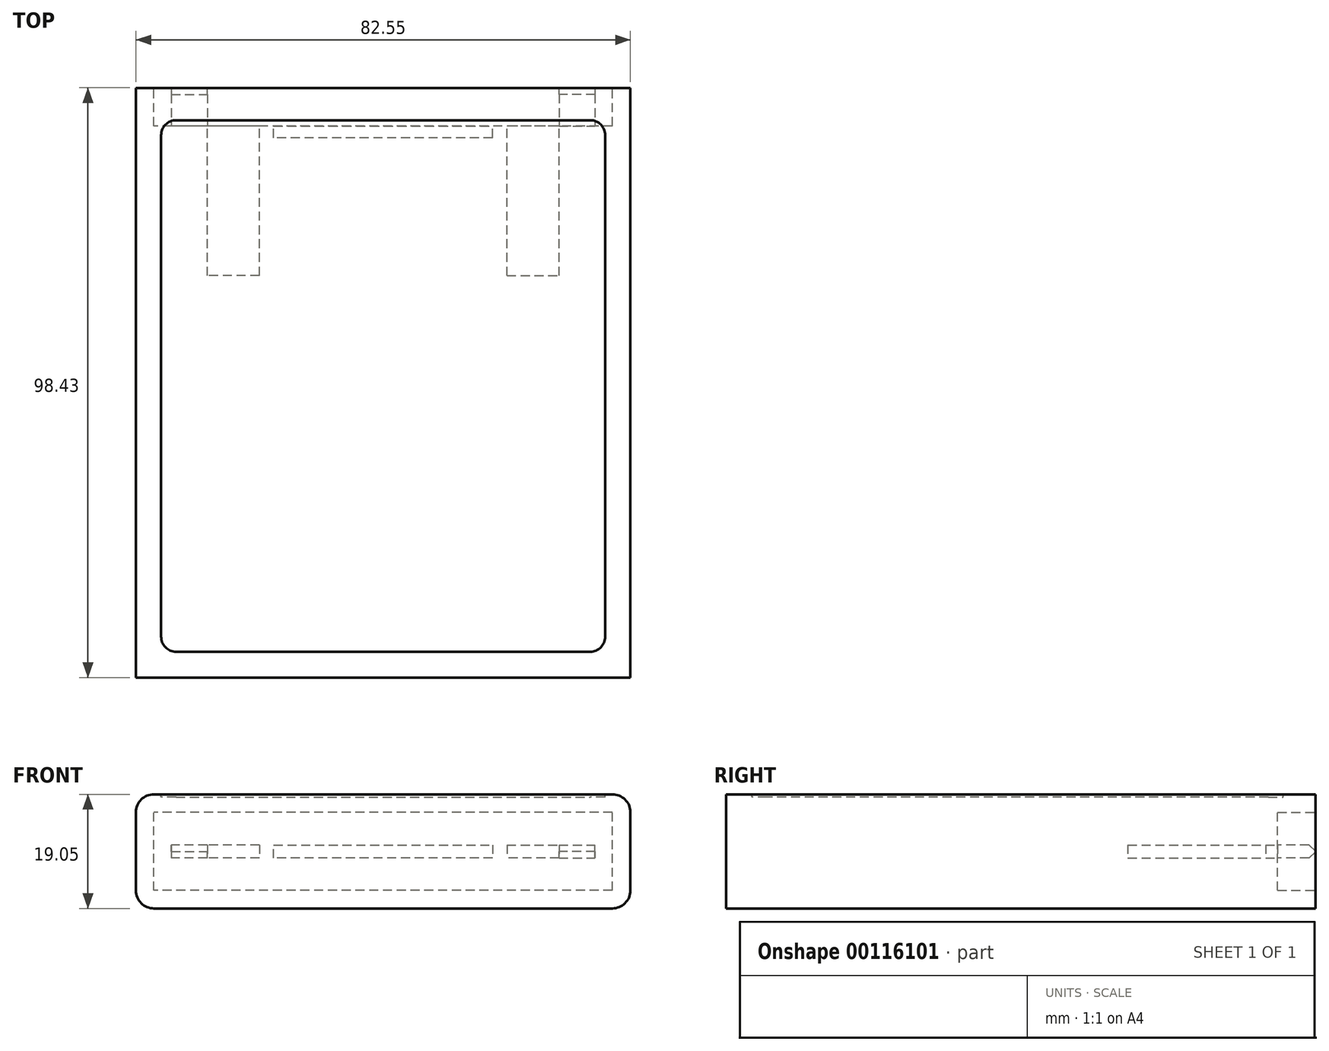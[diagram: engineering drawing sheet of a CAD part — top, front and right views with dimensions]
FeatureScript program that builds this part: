
annotation { "Feature Type Name" : "Feature", "Feature Type Description" : "" }
export const myFeature = defineFeature(function(context is Context, id is Id, definition is map)
    precondition{}
    {
        {
            var Q0;
            Q0=qCreatedBy(makeId("Top.planeOp"),FACE);
            var sketch = newSketch(context, id + "F0", { "sketchPlane" : qUnion([Q0])});
            skLineSegment(sketch, "E0.bottom", {"start": v(0, 0) * mm, "end": v(-82.55, 0) * mm});
            skLineSegment(sketch, "E0.top", {"start": v(0, 98.42) * mm, "end": v(-82.55, 98.42) * mm});
            skLineSegment(sketch, "E0.left", {"start": v(0, 0) * mm, "end": v(0, 98.42) * mm});
            skLineSegment(sketch, "E0.right", {"start": v(-82.55, 0) * mm, "end": v(-82.55, 98.42) * mm});
            skSolve(sketch);
        }
        {
            var Q0;
            Q0=makeQuery(id+"F0.imprint","IMPRINT",FACE,{"disambiguationData":[TD([[makeQuery(id+"F0.imprint","IMPRINT",EDGE,{"derivedFrom":sQuery(id+"F0.wireOp",EDGE,"E0.bottom")}),-1.0]])]});
            var sketch = newSketch(context, id + "F1", { "sketchPlane" : qUnion([Q0])});
            skSolve(sketch);
        }
        {
            var Q0;
            Q0 = qSketchRegion(id + "F1", true);
            var Q1;
            Q1=makeQuery(id+"F0.imprint","IMPRINT",FACE,{"disambiguationData":[TD([[makeQuery(id+"F0.imprint","IMPRINT",EDGE,{"derivedFrom":sQuery(id+"F0.wireOp",EDGE,"E0.bottom")}),-1.0]])]});
            extrude(context, id + "F2", {"entities" : qUnion([Q0, Q1]), "oppositeDirection" : true, "depth" : 19.05 * mm});
        }
        {
            var Q0;
            Q0=makeQuery(id+"F2.opExtrude","CAP_EDGE",EDGE,{"disambiguationData":[OSD([sQuery(id+"F0.wireOp",EDGE,"E0.right")])],"isStart":false});
            var Q1;
            Q1=makeQuery(id+"F2.opExtrude","CAP_EDGE",EDGE,{"disambiguationData":[OSD([sQuery(id+"F0.wireOp",EDGE,"E0.right")])],"isStart":true});
            var Q2;
            Q2=makeQuery(id+"F2.opExtrude","CAP_EDGE",EDGE,{"disambiguationData":[OSD([sQuery(id+"F0.wireOp",EDGE,"E0.left")])],"isStart":true});
            var Q3;
            Q3=makeQuery(id+"F2.opExtrude","CAP_EDGE",EDGE,{"disambiguationData":[OSD([sQuery(id+"F0.wireOp",EDGE,"E0.left")])],"isStart":false});
            fillet(context, id + "F3", {"entities" : qUnion([Q0, Q1, Q2, Q3]), "radius" : 3 * mm, "tangentPropagation" : true, "allowEdgeOverflow" : false});
        }
        {
            var Q0;
            Q0=makeQuery(id+"F2.opExtrude","SWEPT_FACE",FACE,{"disambiguationData":[OSD([sQuery(id+"F0.wireOp",EDGE,"E0.top")])]});
            var sketch = newSketch(context, id + "F4", { "sketchPlane" : qUnion([Q0])});
            skLineSegment(sketch, "E1.bottom", {"start": v(3, -16.05) * mm, "end": v(79.55, -16.05) * mm});
            skLineSegment(sketch, "E1.top", {"start": v(3, -3) * mm, "end": v(79.55, -3) * mm});
            skLineSegment(sketch, "E1.left", {"start": v(3, -16.05) * mm, "end": v(3, -3) * mm});
            skLineSegment(sketch, "E1.right", {"start": v(79.55, -16.05) * mm, "end": v(79.55, -3) * mm});
            skSolve(sketch);
        }
        {
            var Q0;
            Q0 = qSketchRegion(id + "F4", true);
            extrude(context, id + "F5", {"entities" : qUnion([Q0]), "operationType" : NewBodyOperationType.REMOVE, "oppositeDirection" : true, "depth" : 6.35 * mm});
        }
        {
            var Q0;
            Q0=makeQuery(id+"F5.boolean.opBoolean","COPY",FACE,{"derivedFrom":makeQuery(id+"F5.opExtrude","CAP_FACE",FACE,{"disambiguationData":[OSD([sQuery(id+"F4.wireOp",EDGE,"E1.bottom"),sQuery(id+"F4.wireOp",EDGE,"E1.top"),sQuery(id+"F4.wireOp",EDGE,"E1.left"),sQuery(id+"F4.wireOp",EDGE,"E1.right")])],"isStart":false})});
            var sketch = newSketch(context, id + "F6", { "sketchPlane" : qUnion([Q0])});
            skLineSegment(sketch, "E2", {"start": v(23, -10.65) * mm, "end": v(59.55, -10.65) * mm});
            skLineSegment(sketch, "E3", {"start": v(59.55, -10.65) * mm, "end": v(59.55, -8.45) * mm});
            skLineSegment(sketch, "E4", {"start": v(59.55, -8.45) * mm, "end": v(23, -8.45) * mm});
            skLineSegment(sketch, "E5", {"start": v(23, -8.45) * mm, "end": v(23, -10.65) * mm});
            skSolve(sketch);
        }
        {
            var Q0;
            Q0 = qSketchRegion(id + "F6", true);
            extrude(context, id + "F7", {"entities" : qUnion([Q0]), "operationType" : NewBodyOperationType.REMOVE, "oppositeDirection" : true, "depth" : 2 * mm});
        }
        {
            var Q0;
            Q0=makeQuery(id+"F5.boolean.opBoolean","COPY",FACE,{"derivedFrom":makeQuery(id+"F5.opExtrude","CAP_FACE",FACE,{"disambiguationData":[OSD([sQuery(id+"F4.wireOp",EDGE,"E1.bottom"),sQuery(id+"F4.wireOp",EDGE,"E1.top"),sQuery(id+"F4.wireOp",EDGE,"E1.left"),sQuery(id+"F4.wireOp",EDGE,"E1.right")])],"isStart":false})});
            var sketch = newSketch(context, id + "F8", { "sketchPlane" : qUnion([Q0])});
            skPoint(sketch, "E6.firstSnap0", {"position": v(41.27, -8.45) * mm});
            skLineSegment(sketch, "E6.bottom", {"start": v(61.95, -8.45) * mm, "end": v(70.65, -8.45) * mm});
            skLineSegment(sketch, "E6.top", {"start": v(61.95, -10.65) * mm, "end": v(70.65, -10.65) * mm});
            skLineSegment(sketch, "E6.left", {"start": v(61.95, -8.45) * mm, "end": v(61.95, -10.65) * mm});
            skLineSegment(sketch, "E6.right", {"start": v(70.65, -8.45) * mm, "end": v(70.65, -10.65) * mm});
            skPoint(sketch, "E7.firstSnap0", {"position": v(66.3, -8.45) * mm});
            skLineSegment(sketch, "E7.bottom", {"start": v(20.6, -8.45) * mm, "end": v(11.9, -8.45) * mm});
            skLineSegment(sketch, "E7.left", {"start": v(20.6, -8.45) * mm, "end": v(20.6, -10.65) * mm});
            skLineSegment(sketch, "E7.right", {"start": v(11.9, -8.45) * mm, "end": v(11.9, -10.65) * mm});
            skLineSegment(sketch, "E8", {"start": v(11.9, -10.65) * mm, "end": v(20.6, -10.65) * mm});
            skSolve(sketch);
        }
        {
            var Q0;
            Q0 = qSketchRegion(id + "F8", true);
            extrude(context, id + "F9", {"entities" : qUnion([Q0]), "operationType" : NewBodyOperationType.REMOVE, "oppositeDirection" : true, "depth" : 25 * mm});
        }
        {
            var Q0;
            Q0=makeQuery(id+"F5.boolean.opBoolean","COPY",FACE,{"derivedFrom":makeQuery(id+"F5.opExtrude","CAP_FACE",FACE,{"disambiguationData":[OSD([sQuery(id+"F4.wireOp",EDGE,"E1.bottom"),sQuery(id+"F4.wireOp",EDGE,"E1.top"),sQuery(id+"F4.wireOp",EDGE,"E1.left"),sQuery(id+"F4.wireOp",EDGE,"E1.right")])],"isStart":false})});
            var sketch = newSketch(context, id + "F10", { "sketchPlane" : qUnion([Q0])});
            skLineSegment(sketch, "E9.bottom", {"start": v(70.65, -8.45) * mm, "end": v(76.65, -8.45) * mm});
            skLineSegment(sketch, "E9.top", {"start": v(70.65, -10.65) * mm, "end": v(76.65, -10.65) * mm});
            skLineSegment(sketch, "E9.left", {"start": v(70.65, -8.45) * mm, "end": v(70.65, -10.65) * mm});
            skLineSegment(sketch, "E9.right", {"start": v(76.65, -8.45) * mm, "end": v(76.65, -10.65) * mm});
            skLineSegment(sketch, "E10.bottom", {"start": v(11.9, -10.65) * mm, "end": v(5.9, -10.65) * mm});
            skLineSegment(sketch, "E10.top", {"start": v(11.9, -8.45) * mm, "end": v(5.9, -8.45) * mm});
            skLineSegment(sketch, "E10.left", {"start": v(11.9, -10.65) * mm, "end": v(11.9, -8.45) * mm});
            skLineSegment(sketch, "E10.right", {"start": v(5.9, -10.65) * mm, "end": v(5.9, -8.45) * mm});
            skSolve(sketch);
        }
        {
            var Q0;
            Q0 = qSketchRegion(id + "F10", true);
            var Q1;
            Q1=makeQuery(id+"F2.opExtrude","SWEPT_FACE",FACE,{"disambiguationData":[OSD([sQuery(id+"F0.wireOp",EDGE,"E0.top")])]});
            extrude(context, id + "F11", {"entities" : qUnion([Q0]), "operationType" : NewBodyOperationType.ADD, "endBound" : BoundingType.UP_TO_SURFACE, "endBoundEntityFace" : qUnion([Q1]), "depth" : 25 * mm});
        }
        {
            var Q0;
            Q0=makeQuery(id+"F11.opExtrude","CAP_EDGE",EDGE,{"disambiguationData":[OSD([sQuery(id+"F10.wireOp",EDGE,"E10.top")])],"isStart":false});
            var Q1;
            Q1=makeQuery(id+"F11.opExtrude","CAP_EDGE",EDGE,{"disambiguationData":[OSD([sQuery(id+"F10.wireOp",EDGE,"E10.bottom")])],"isStart":false});
            var Q2;
            Q2=makeQuery(id+"F11.opExtrude","CAP_EDGE",EDGE,{"disambiguationData":[OSD([sQuery(id+"F10.wireOp",EDGE,"E9.bottom")])],"isStart":false});
            var Q3;
            Q3=makeQuery(id+"F11.opExtrude","CAP_EDGE",EDGE,{"disambiguationData":[OSD([sQuery(id+"F10.wireOp",EDGE,"E9.top")])],"isStart":false});
            chamfer(context, id + "F12", {"entities" : qUnion([Q0, Q1, Q2, Q3]), "width" : 1.1 * mm, "tangentPropagation" : true});
        }
        {
            var Q0;
            Q0=makeQuery(id+"F1.imprint","IMPRINT",FACE,{"disambiguationData":[TD([[makeQuery(id+"F1.imprint","IMPRINT",EDGE,{"derivedFrom":makeQuery(id+"F0.imprint","IMPRINT",EDGE,{"derivedFrom":sQuery(id+"F0.wireOp",EDGE,"E0.bottom")})}),-1.0]])]});
            var sketch = newSketch(context, id + "F13", { "sketchPlane" : qUnion([Q0])});
            skLineSegment(sketch, "E11", {"start": v(-75.85, 93.02) * mm, "end": v(-6.7, 93.02) * mm});
            skLineSegment(sketch, "E12", {"start": v(-4.2, 90.52) * mm, "end": v(-4.2, 6.8) * mm});
            skLineSegment(sketch, "E13", {"start": v(-6.7, 4.3) * mm, "end": v(-75.85, 4.3) * mm});
            skLineSegment(sketch, "E14", {"start": v(-78.35, 90.52) * mm, "end": v(-78.35, 6.8) * mm});
            skArc(sketch, "E15", {"start": v(-78.35, 90.52) * mm, "mid": v(-77.62, 92.3) * mm, "end": v(-75.85, 93.02) * mm});
            skArc(sketch, "E16", {"start": v(-6.7, 93.02) * mm, "mid": v(-4.93, 92.3) * mm, "end": v(-4.2, 90.52) * mm});
            skArc(sketch, "E17", {"start": v(-4.2, 6.8) * mm, "mid": v(-4.93, 5.03) * mm, "end": v(-6.7, 4.3) * mm});
            skArc(sketch, "E18", {"start": v(-75.85, 4.3) * mm, "mid": v(-77.62, 5.03) * mm, "end": v(-78.35, 6.8) * mm});
            skSolve(sketch);
        }
        {
            var Q0;
            Q0 = qSketchRegion(id + "F13", true);
            extrude(context, id + "F14", {"entities" : qUnion([Q0]), "operationType" : NewBodyOperationType.REMOVE, "oppositeDirection" : true, "depth" : .5 * mm});
        }
    });
